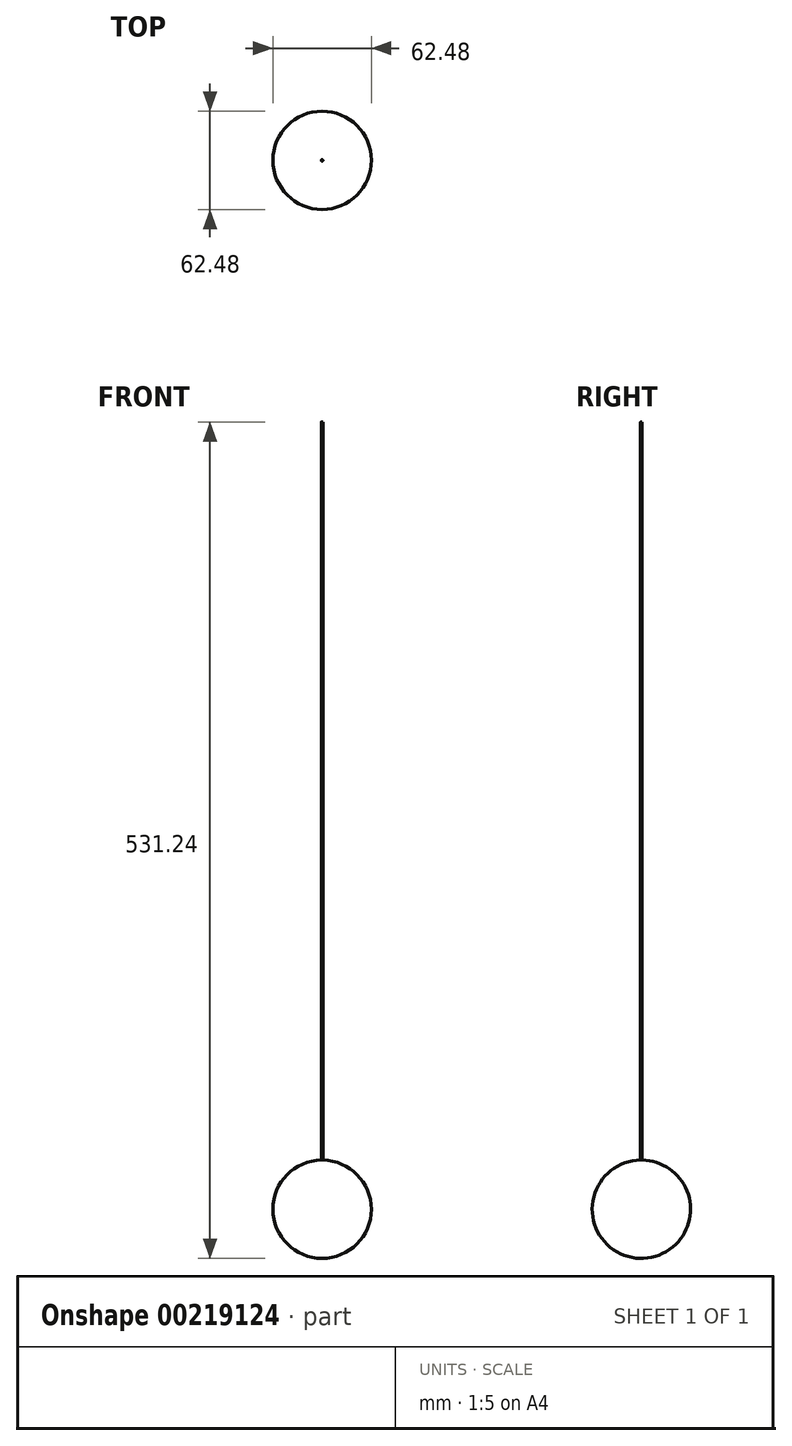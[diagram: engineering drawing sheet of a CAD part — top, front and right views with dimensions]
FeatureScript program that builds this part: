
annotation { "Feature Type Name" : "Feature", "Feature Type Description" : "" }
export const myFeature = defineFeature(function(context is Context, id is Id, definition is map)
    precondition{}
    {
        {
            var Q0;
            Q0=qCreatedBy(makeId("Top.planeOp"),FACE);
            var sketch = newSketch(context, id + "F0", { "sketchPlane" : qUnion([Q0])});
            skArc(sketch, "E0", {"start": v(31.24, 0) * mm, "mid": v(0, 31.24) * mm, "end": v(-31.24, 0) * mm});
            skLineSegment(sketch, "E1", {"start": v(0, 0) * mm, "end": v(-31.24, 0) * mm});
            skLineSegment(sketch, "E2", {"start": v(0, 0) * mm, "end": v(31.24, 0) * mm});
            skSolve(sketch);
        }
        {
            var Q0;
            Q0=makeQuery(id+"F0.imprint","IMPRINT",FACE,{"disambiguationData":[TD([[makeQuery(id+"F0.imprint","IMPRINT",EDGE,{"derivedFrom":sQuery(id+"F0.wireOp",EDGE,"E0")}),1.0]])]});
            var Q1;
            Q1=sQuery(id+"F0.wireOp",EDGE,"E2");
            revolve(context, id + "F1", {"entities" : qUnion([Q0]), "axis" : qUnion([Q1]), "revolveType" : RevolveType.FULL});
        }
        {
            var Q0;
            Q0=qCreatedBy(makeId("Top.planeOp"),FACE);
            var sketch = newSketch(context, id + "F2", { "sketchPlane" : qUnion([Q0])});
            skCircle(sketch, "E3", {"center": v(0, 0) * mm, "radius": 0.5 * mm});
            skSolve(sketch);
        }
        {
            var Q0;
            Q0=makeQuery(id+"F2.imprint","IMPRINT",FACE,{"disambiguationData":[TD([[makeQuery(id+"F2.imprint","IMPRINT",EDGE,{"derivedFrom":sQuery(id+"F2.wireOp",EDGE,"E3")}),1.0]])]});
            extrude(context, id + "F3", {"entities" : qUnion([Q0]), "operationType" : NewBodyOperationType.ADD, "depth" : 500 * mm});
        }
    });
